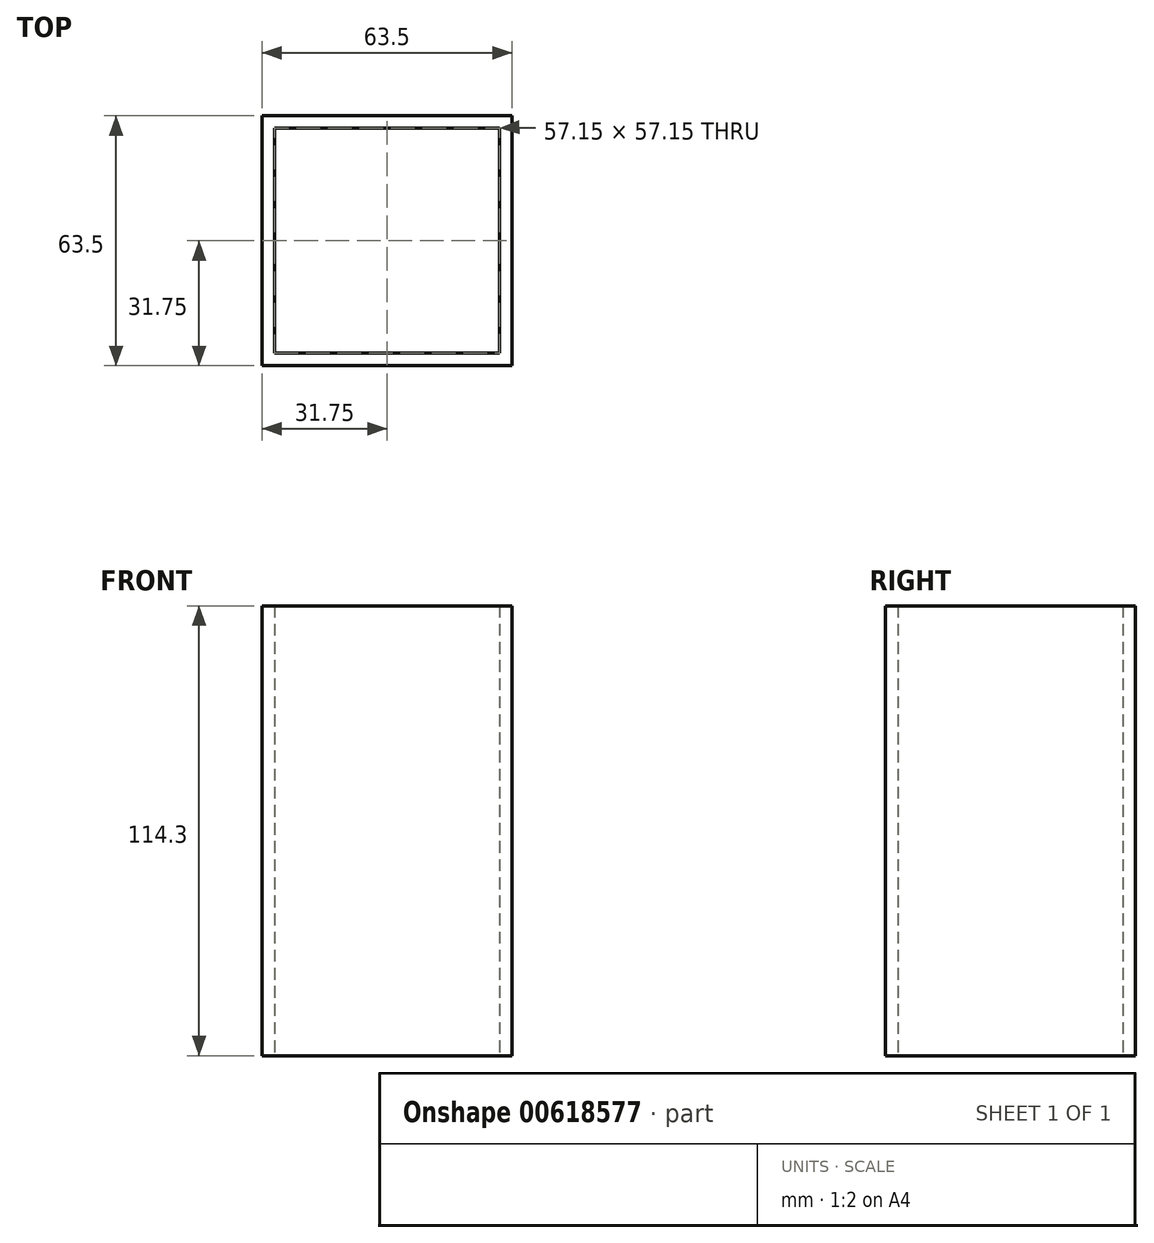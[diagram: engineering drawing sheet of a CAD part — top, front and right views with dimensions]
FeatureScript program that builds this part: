
annotation { "Feature Type Name" : "Feature", "Feature Type Description" : "" }
export const myFeature = defineFeature(function(context is Context, id is Id, definition is map)
    precondition{}
    {
        {
            var Q0;
            Q0=qCreatedBy(makeId("Top.planeOp"),FACE);
            var sketch = newSketch(context, id + "F0", { "sketchPlane" : qUnion([Q0])});
            skLineSegment(sketch, "E0.bottom", {"start": v(31.75, -31.75) * mm, "end": v(-31.75, -31.75) * mm});
            skLineSegment(sketch, "E0.top", {"start": v(31.75, 31.75) * mm, "end": v(-31.75, 31.75) * mm});
            skLineSegment(sketch, "E0.left", {"start": v(31.75, -31.75) * mm, "end": v(31.75, 31.75) * mm});
            skLineSegment(sketch, "E0.right", {"start": v(-31.75, -31.75) * mm, "end": v(-31.75, 31.75) * mm});
            skPoint(sketch, "E0.middle", {"position": v(0, 0) * mm});
            skLineSegment(sketch, "E1.bottom", {"start": v(28.58, -28.58) * mm, "end": v(-28.58, -28.58) * mm});
            skLineSegment(sketch, "E1.top", {"start": v(28.58, 28.58) * mm, "end": v(-28.58, 28.58) * mm});
            skLineSegment(sketch, "E1.left", {"start": v(28.58, -28.58) * mm, "end": v(28.58, 28.58) * mm});
            skLineSegment(sketch, "E1.right", {"start": v(-28.58, -28.58) * mm, "end": v(-28.58, 28.57) * mm});
            skSolve(sketch);
        }
        {
            var Q0;
            Q0 = qSketchRegion(id + "F0", true);
            extrude(context, id + "F1", {"entities" : qUnion([Q0]), "depth" : 114.3 * mm, "offsetDistance" : 25.4 * mm});
        }
    });
